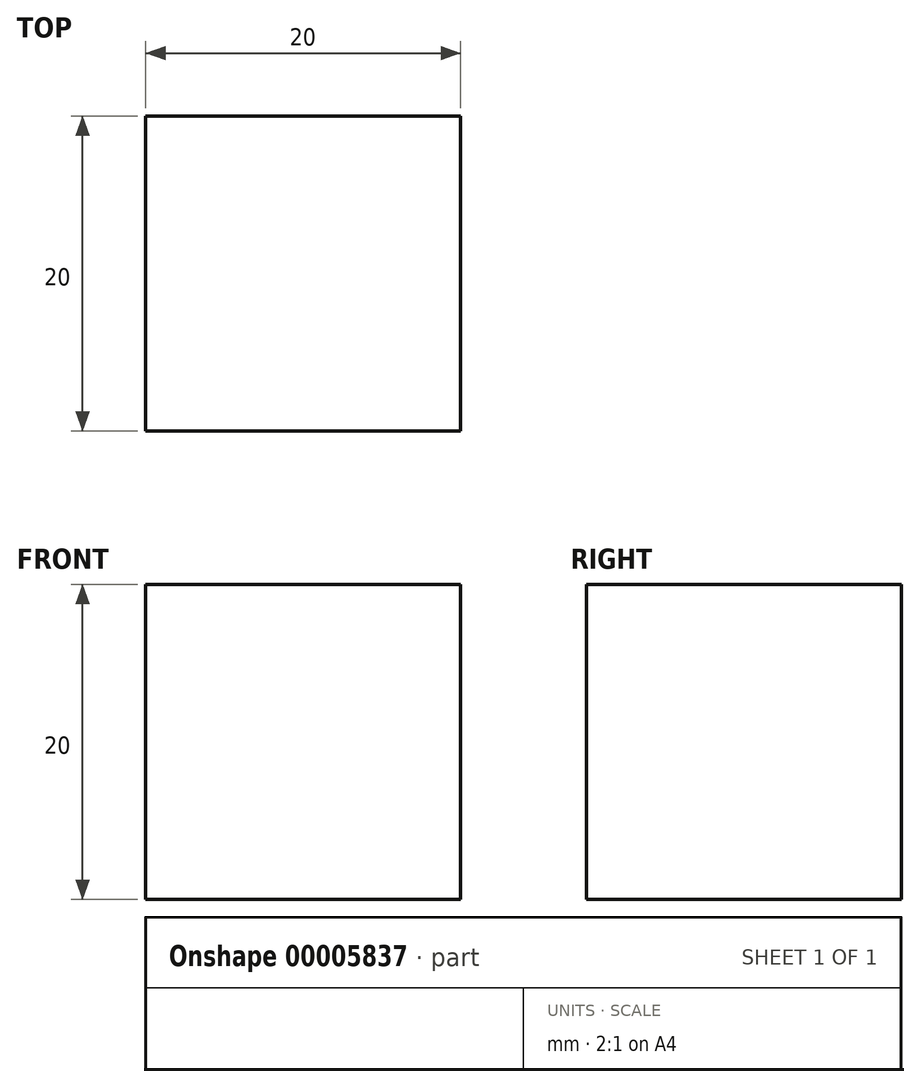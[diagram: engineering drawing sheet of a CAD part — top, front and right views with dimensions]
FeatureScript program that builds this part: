
annotation { "Feature Type Name" : "Feature", "Feature Type Description" : "" }
export const myFeature = defineFeature(function(context is Context, id is Id, definition is map)
    precondition{}
    {
        {
            var Q0;
            Q0=qCreatedBy(makeId("Top.planeOp"),FACE);
            var sketch = newSketch(context, id + "F0", { "sketchPlane" : qUnion([Q0])});
            skLineSegment(sketch, "E0.bottom", {"start": v(10, -10) * mm, "end": v(-10, -10) * mm});
            skLineSegment(sketch, "E0.top", {"start": v(10, 10) * mm, "end": v(-10, 10) * mm});
            skLineSegment(sketch, "E0.left", {"start": v(10, -10) * mm, "end": v(10, 10) * mm});
            skLineSegment(sketch, "E0.right", {"start": v(-10, -10) * mm, "end": v(-10, 10) * mm});
            skPoint(sketch, "E0.middle", {"position": v(0, 0) * mm});
            skSolve(sketch);
        }
        {
            var Q0;
            Q0=makeQuery(id+"F0.imprint","IMPRINT",FACE,{"disambiguationData":[TD([[makeQuery(id+"F0.imprint","IMPRINT",EDGE,{"derivedFrom":sQuery(id+"F0.wireOp",EDGE,"E0.bottom")}),-1.0]])]});
            extrude(context, id + "F1", {"entities" : qUnion([Q0]), "depth" : 20 * mm, "offsetDistance" : 25 * mm});
        }
    });
